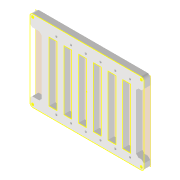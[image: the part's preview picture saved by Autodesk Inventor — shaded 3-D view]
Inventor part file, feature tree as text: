
AUTODESK INVENTOR PART (.ipt)
format: ipt  version: 2022 (Build 260153000, 153)  size: 570,368 bytes
history: native  units: mm
features: reference x5, sketch x4, other x4, extrude x3, projected_geometry x2, plane x1, pattern_linear x1, fillet x1, chamfer x1
ambient origin geometry x8: Origin, YZ Plane, XZ Plane, XY Plane, X Axis, Y Axis, Z Axis, Center Point
bodies: Volumenkörper1 (feature_tree)
feature tree (22):
  plane  "Arbeitsebene1"
  extrude  "Extrusion1"  Depth=3.5mm
  extrude  "Extrusion2"  Depth=2.8mm
  pattern_linear  "Rechteckige Anordnung1"  Spacing1=8.0mm  [1 undecoded]
  fillet  "Rundung1"  Radius=1.0mm
  sketch  "Skizze3"  dims[d4=2.8mm]
  extrude  "Extrusion3"  Depth=15.0mm
  chamfer  "Fase1"  Distance=0.5mm
  sketch  "Skizze1"  dims[d0=6.0mm d1=3.5mm]
  reference  "Referenz1"
  sketch  "Skizze2"  dims[d2=2.8mm d3=2.8mm]
  reference  "Referenz2"
  reference  "Referenz3"
  reference  "Referenz4"
  projected_geometry  "Projizierte Kontur1"
  sketch  "Skizze4"  dims[d5=3.0mm d6=8.0mm d7=0.0mm d8=1.0mm d9=1.0mm d11=0.5mm d12=8.4mm d13=0.0mm d14=0.0mm d15=60.0mm d17=18.7mm d18=4.0mm d19=2.8mm d20=2.8mm d21=5.0mm d22=5.0mm d23=10.0mm d24=15.0mm d25=0.0mm d26=0.0mm d27=3.0mm d28=2.0mm d29=45.0deg]
  projected_geometry  "Projizierte Kontur2"
  reference  "Referenz5"
  other  "Baugruppe1"
  other  "00_Omniscope_PCB_USBC:1"
  other  "00_Seeeduino Xiao:19"
  other  "00_Seeeduino Xiao:1"
note: 1 required parameter value undecoded (feature->parameter linkage not recoverable at this tier; creation-order binding heuristic only, values carry confidence <= 0.55)
